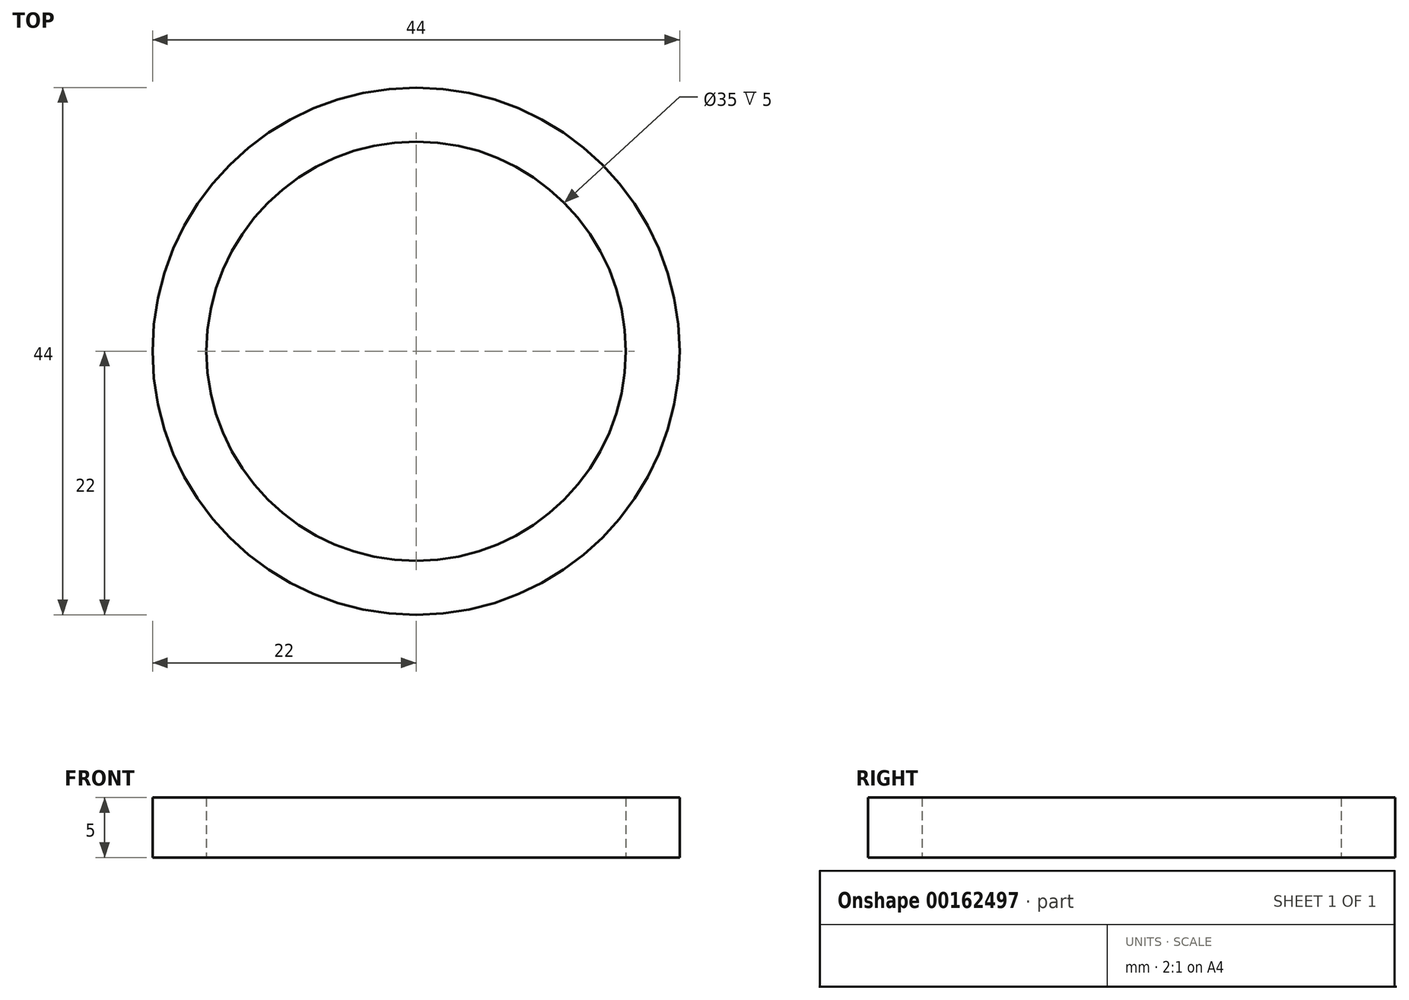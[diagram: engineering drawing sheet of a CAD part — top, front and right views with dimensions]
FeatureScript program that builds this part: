
annotation { "Feature Type Name" : "Feature", "Feature Type Description" : "" }
export const myFeature = defineFeature(function(context is Context, id is Id, definition is map)
    precondition{}
    {
        {
            var Q0;
            Q0=qCreatedBy(makeId("Top.planeOp"),FACE);
            var sketch = newSketch(context, id + "F0", { "sketchPlane" : qUnion([Q0])});
            skCircle(sketch, "E0", {"center": v(0, 0) * mm, "radius": 22 * mm});
            skCircle(sketch, "E1", {"center": v(0, 0) * mm, "radius": 17.5 * mm});
            skSolve(sketch);
        }
        {
            var Q0;
            Q0 = qSketchRegion(id + "F0", true);
            extrude(context, id + "F1", {"entities" : qUnion([Q0]), "depth" : 5 * mm});
        }
    });
